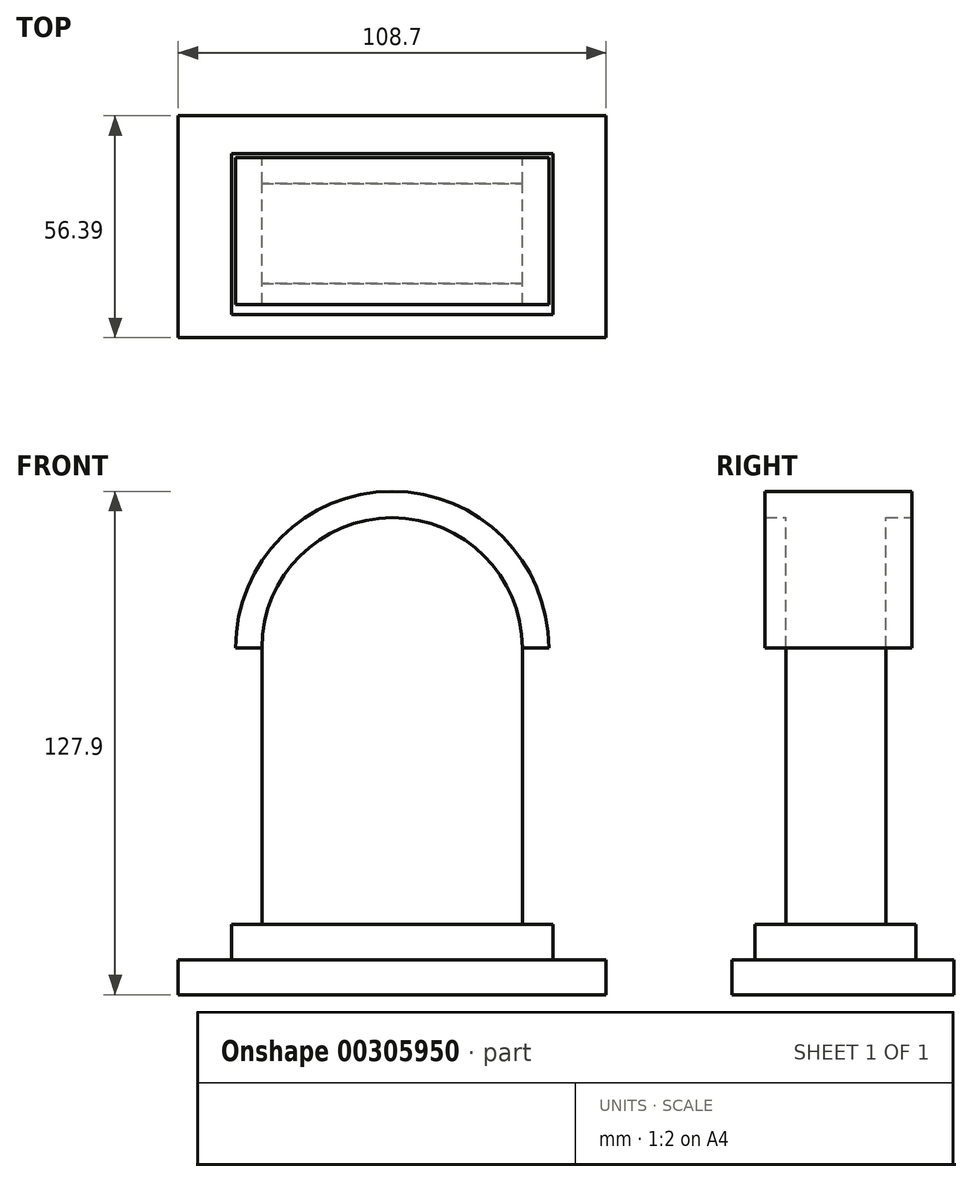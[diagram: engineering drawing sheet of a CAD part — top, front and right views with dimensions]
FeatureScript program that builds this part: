
annotation { "Feature Type Name" : "Feature", "Feature Type Description" : "" }
export const myFeature = defineFeature(function(context is Context, id is Id, definition is map)
    precondition{}
    {
        {
            var Q0;
            Q0=qCreatedBy(makeId("Front.planeOp"),FACE);
            var sketch = newSketch(context, id + "F0", { "sketchPlane" : qUnion([Q0])});
            skLineSegment(sketch, "E0.bottom", {"start": v(-33.08, 44.22) * mm, "end": v(33.08, 44.22) * mm});
            skLineSegment(sketch, "E0.top", {"start": v(-33.08, -44.22) * mm, "end": v(33.08, -44.22) * mm});
            skLineSegment(sketch, "E0.left", {"start": v(-33.08, 44.22) * mm, "end": v(-33.08, -44.22) * mm});
            skLineSegment(sketch, "E0.right", {"start": v(33.08, 44.22) * mm, "end": v(33.08, -44.22) * mm});
            skPoint(sketch, "E0.middle", {"position": v(0, 0) * mm});
            skArc(sketch, "E1", {"start": v(33.08, 44.22) * mm, "mid": v(0, 77.3) * mm, "end": v(-33.08, 44.22) * mm});
            skLineSegment(sketch, "E2.bottom", {"start": v(-40.85, -44.22) * mm, "end": v(40.85, -44.22) * mm});
            skLineSegment(sketch, "E2.top", {"start": v(-40.85, -26) * mm, "end": v(40.85, -26) * mm});
            skLineSegment(sketch, "E2.left", {"start": v(-40.85, -44.22) * mm, "end": v(-40.85, -26) * mm});
            skLineSegment(sketch, "E2.right", {"start": v(40.85, -44.22) * mm, "end": v(40.85, -26) * mm});
            skPoint(sketch, "E2.middle", {"position": v(0, -35.11) * mm});
            skPoint(sketch, "E2.middle.positionSnap0", {"position": v(0, -44.22) * mm});
            skPoint(sketch, "E2.cornerSnap0", {"position": v(0, -44.22) * mm});
            skPoint(sketch, "E2.centerSnap0", {"position": v(0, -44.22) * mm});
            skLineSegment(sketch, "E3.bottom", {"start": v(-54.35, -35.11) * mm, "end": v(54.35, -35.11) * mm});
            skLineSegment(sketch, "E3.top", {"start": v(-54.35, -43.89) * mm, "end": v(54.35, -43.89) * mm});
            skLineSegment(sketch, "E3.left", {"start": v(-54.35, -35.11) * mm, "end": v(-54.35, -43.89) * mm});
            skLineSegment(sketch, "E3.right", {"start": v(54.35, -35.11) * mm, "end": v(54.35, -43.89) * mm});
            skPoint(sketch, "E3.middle", {"position": v(0, -39.5) * mm});
            skPoint(sketch, "E3.cornerSnap0", {"position": v(-40.85, -35.11) * mm});
            skArc(sketch, "E4", {"start": v(-39.79, 44.22) * mm, "mid": v(0, 84) * mm, "end": v(39.79, 44.22) * mm});
            skLineSegment(sketch, "E5", {"start": v(-39.79, 44.22) * mm, "end": v(-33.08, 44.22) * mm});
            skLineSegment(sketch, "E6", {"start": v(33.08, 44.22) * mm, "end": v(39.79, 44.22) * mm});
            skSolve(sketch);
        }
        {
            var Q0;
            Q0=makeQuery(id+"F0.imprint","IMPRINT",FACE,{"disambiguationData":[TD([[makeQuery(id+"F0.imprint","IMPRINT",EDGE,{"derivedFrom":sQuery(id+"F0.wireOp",EDGE,"E0.bottom")}),1.0]])]});
            var Q1;
            {var subQ0=sQuery(id+"F0.wireOp",EDGE,"E0.bottom");Q1=makeQuery(id+"F0.imprint","IMPRINT",FACE,{"disambiguationData":[TD([[makeQuery(id+"F0.imprint","IMPRINT",EDGE,{"derivedFrom":subQ0}),-1.0]])]});}
            extrude(context, id + "F1", {"entities" : qUnion([Q0, Q1]), "depth" : 25.4 * mm});
        }
        {
            var Q0;
            Q0=makeQuery(id+"F0.imprint","IMPRINT",FACE,{"disambiguationData":[TD([[makeQuery(id+"F0.imprint","IMPRINT",EDGE,{"derivedFrom":sQuery(id+"F0.wireOp",EDGE,"E1")}),-1.0]])]});
            extrude(context, id + "F2", {"entities" : qUnion([Q0]), "operationType" : NewBodyOperationType.ADD, "depth" : 30.73 * mm, "hasSecondDirection" : true, "secondDirectionOppositeDirection" : true, "secondDirectionDepth" : 6.6 * mm});
        }
        {
            var Q0;
            {var subQ0=sQuery(id+"F0.wireOp",EDGE,"E2.top");var subQ1=sQuery(id+"F0.wireOp",EDGE,"E0.right");var subQ2=makeQuery(id+"F0.imprint","INTERSECT",VERTEX,{"derivedFrom":[subQ1,subQ0]});Q0=makeQuery(id+"F0.imprint","IMPRINT",FACE,{"disambiguationData":[TD([[makeQuery(id+"F0.imprint","IMPRINT",EDGE,{"disambiguationData":[TD([[subQ2,-1.0]])],"derivedFrom":subQ1}),1.0]])]});}
            var Q1;
            {var subQ0=sQuery(id+"F0.wireOp",EDGE,"E2.top");var subQ1=sQuery(id+"F0.wireOp",EDGE,"E0.left");var subQ2=makeQuery(id+"F0.imprint","INTERSECT",VERTEX,{"derivedFrom":[subQ1,subQ0]});Q1=makeQuery(id+"F0.imprint","IMPRINT",FACE,{"disambiguationData":[TD([[makeQuery(id+"F0.imprint","IMPRINT",EDGE,{"disambiguationData":[TD([[subQ2,-1.0]])],"derivedFrom":subQ1}),1.0]])]});}
            var Q2;
            {var subQ0=sQuery(id+"F0.wireOp",EDGE,"E2.top");var subQ1=sQuery(id+"F0.wireOp",EDGE,"E0.left");var subQ2=makeQuery(id+"F0.imprint","INTERSECT",VERTEX,{"derivedFrom":[subQ1,subQ0]});Q2=makeQuery(id+"F0.imprint","IMPRINT",FACE,{"disambiguationData":[TD([[makeQuery(id+"F0.imprint","IMPRINT",EDGE,{"disambiguationData":[TD([[subQ2,-1.0]])],"derivedFrom":subQ1}),-1.0]])]});}
            extrude(context, id + "F3", {"entities" : qUnion([Q0, Q1, Q2]), "operationType" : NewBodyOperationType.ADD, "depth" : 33.27 * mm, "hasSecondDirection" : true, "secondDirectionOppositeDirection" : true, "secondDirectionDepth" : 7.62 * mm});
        }
        {
            var Q0;
            {var subQ5=sQuery(id+"F0.wireOp",EDGE,"E3.right");Q0=makeQuery(id+"F0.imprint","IMPRINT",FACE,{"disambiguationData":[TD([[makeQuery(id+"F0.imprint","IMPRINT",EDGE,{"derivedFrom":subQ5}),-1.0]])]});}
            var Q1;
            {var subQ0=sQuery(id+"F0.wireOp",EDGE,"E3.bottom");var subQ1=sQuery(id+"F0.wireOp",EDGE,"E0.right");var subQ2=makeQuery(id+"F0.imprint","INTERSECT",VERTEX,{"derivedFrom":[subQ1,subQ0]});Q1=makeQuery(id+"F0.imprint","IMPRINT",FACE,{"disambiguationData":[TD([[makeQuery(id+"F0.imprint","IMPRINT",EDGE,{"disambiguationData":[TD([[subQ2,-1.0]])],"derivedFrom":subQ1}),1.0]])]});}
            var Q2;
            {var subQ0=sQuery(id+"F0.wireOp",EDGE,"E3.bottom");var subQ1=sQuery(id+"F0.wireOp",EDGE,"E0.left");var subQ2=makeQuery(id+"F0.imprint","INTERSECT",VERTEX,{"derivedFrom":[subQ1,subQ0]});Q2=makeQuery(id+"F0.imprint","IMPRINT",FACE,{"disambiguationData":[TD([[makeQuery(id+"F0.imprint","IMPRINT",EDGE,{"disambiguationData":[TD([[subQ2,-1.0]])],"derivedFrom":subQ1}),1.0]])]});}
            var Q3;
            {var subQ0=sQuery(id+"F0.wireOp",EDGE,"E3.bottom");var subQ1=sQuery(id+"F0.wireOp",EDGE,"E0.left");var subQ2=makeQuery(id+"F0.imprint","INTERSECT",VERTEX,{"derivedFrom":[subQ1,subQ0]});Q3=makeQuery(id+"F0.imprint","IMPRINT",FACE,{"disambiguationData":[TD([[makeQuery(id+"F0.imprint","IMPRINT",EDGE,{"disambiguationData":[TD([[subQ2,-1.0]])],"derivedFrom":subQ1}),-1.0]])]});}
            var Q4;
            {var subQ5=sQuery(id+"F0.wireOp",EDGE,"E3.left");Q4=makeQuery(id+"F0.imprint","IMPRINT",FACE,{"disambiguationData":[TD([[makeQuery(id+"F0.imprint","IMPRINT",EDGE,{"derivedFrom":subQ5}),1.0]])]});}
            extrude(context, id + "F4", {"entities" : qUnion([Q0, Q1, Q2, Q3, Q4]), "operationType" : NewBodyOperationType.ADD, "depth" : 39.12 * mm, "hasSecondDirection" : true, "secondDirectionOppositeDirection" : true, "secondDirectionDepth" : 17.27 * mm});
        }
        {
            var Q0;
            Q0=makeQuery(id+"F1.opExtrude","CAP_FACE",FACE,{"disambiguationData":[OSD([sQuery(id+"F0.wireOp",EDGE,"E0.left"),sQuery(id+"F0.wireOp",EDGE,"E0.right"),sQuery(id+"F0.wireOp",EDGE,"E1"),sQuery(id+"F0.wireOp",EDGE,"E2.top")])],"isStart":false});
            var sketch = newSketch(context, id + "F5", { "sketchPlane" : qUnion([Q0])});
            skText(sketch, "E7", { "text": "R.I.P", "fontName": "OpenSans-Bold.ttf"});
            const initialGuessF5  = {"E7": [-0.02727, 0.04432, 1, 0, 0.01818]};
            skSetInitialGuess(sketch, initialGuessF5);
            skSolve(sketch);
        }
    });
